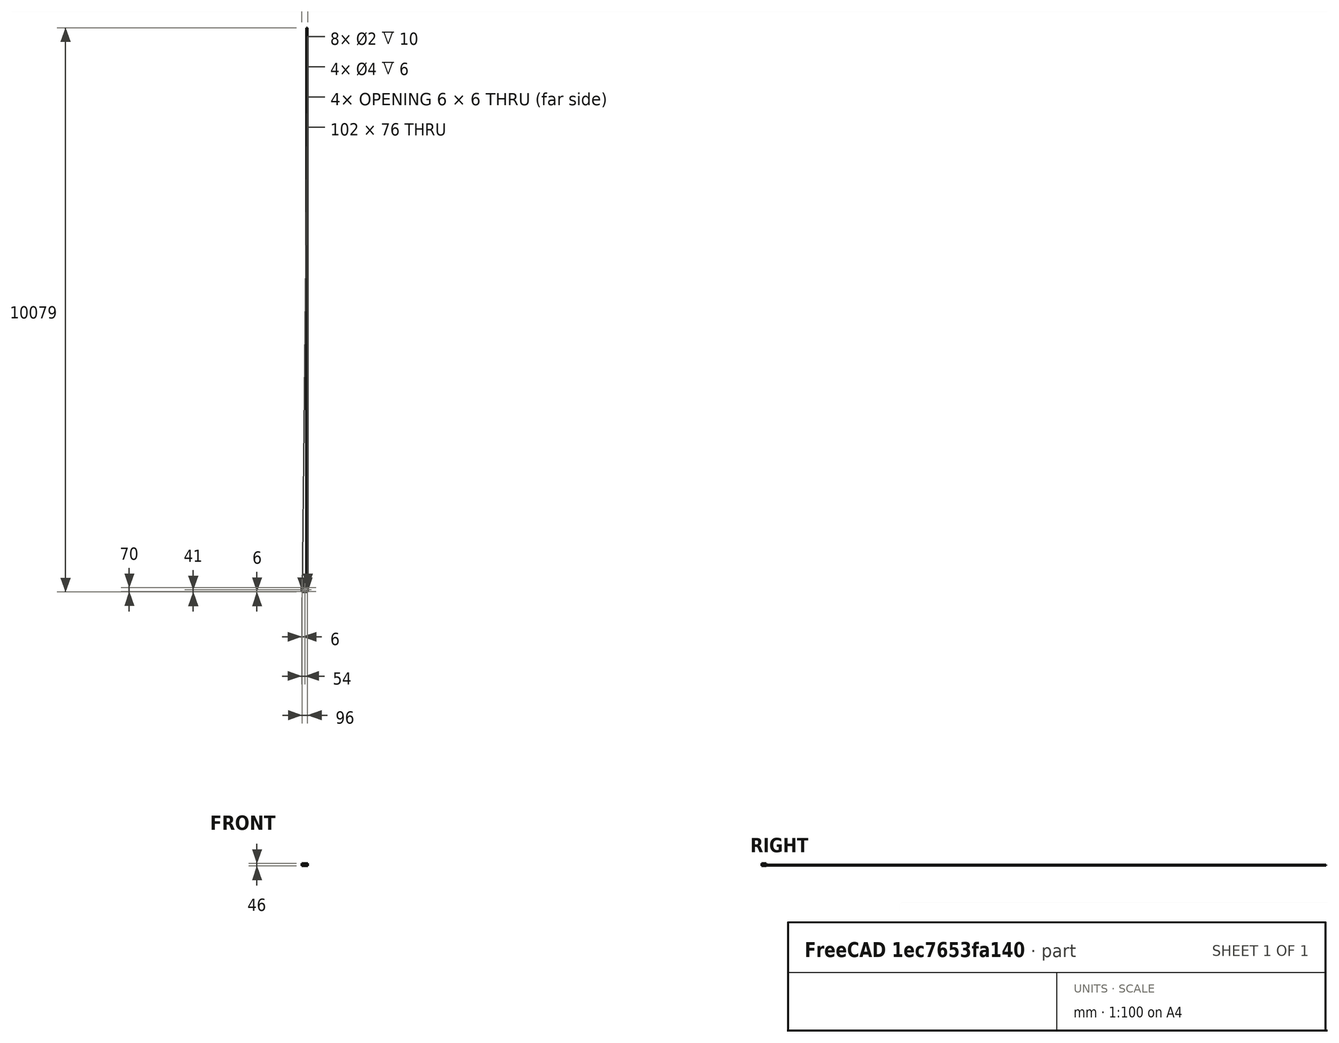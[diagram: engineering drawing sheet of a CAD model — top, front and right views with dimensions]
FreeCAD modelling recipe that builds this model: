
FCSTD DOCUMENT  (FreeCAD 0.16R6712 (Git))
Label: DMX_RGB_BOX
License: All rights reserved
LicenseURL: http://en.wikipedia.org/wiki/All_rights_reserved
objects: Part::Box×5, Part::Cut×5, Part::Cylinder×4, PartDesign::Chamfer×3, Part::Fillet×3, Sketcher::SketchObject×2, PartDesign::Pocket×2, PartDesign::Fillet×1, Part::MultiFuse×1, Mesh::Feature×1
note: 28 computed .brp shape members not serialized (recipe doc carries the construction recipe); baked Part::Feature solids carry a one-line shape summary decoded from their .brp

FEATURE [PartDesign::Chamfer] Chamfer  label="Deckel"
  Placement = pos=(0,82,46) rot=(1,0,0;3.14159rad)
  Size = 2
FEATURE [Part::Box] Box  label="Würfel"
  Height = 43
  Length = 108
  Width = 82
FEATURE [Part::Box] Box001  label="Würfel001"
  Height = 41
  Length = 102
  Placement = pos=(3,3,3) rot=(0,0,1;0rad)
  Width = 76
FEATURE [Part::Cut] Cut
  Base = -> Box
  Tool = -> Box001
FEATURE [PartDesign::Fillet] Fillet
  Placement = pos=(3,3,0) rot=(0,0,1;0rad)
  Radius = 3
FEATURE [Part::Box] Box003  label="Würfel003"
  Height = 35
  Length = 6
  Placement = pos=(3,73,0) rot=(0,0,1;0rad)
  Width = 6
FEATURE [Part::Box] Box004  label="Würfel004"
  Height = 35
  Length = 6
  Placement = pos=(99,3,0) rot=(0,0,1;0rad)
  Width = 6
FEATURE [Part::Box] Box005  label="Würfel005"
  Height = 35
  Length = 6
  Placement = pos=(99,73,0) rot=(0,0,1;0rad)
  Width = 6
FEATURE [Part::Fillet] Fillet001
  Base = -> Box003
  Edges = 1 edges r=3: [Edge5]
FEATURE [Part::Fillet] Fillet002
  Base = -> Box004
  Edges = 1 edges r=3: [Edge3]
FEATURE [Part::Fillet] Fillet003
  Base = -> Box005
  Edges = 1 edges r=3: [Edge1]
FEATURE [Part::Cylinder] Cylinder  label="Zylinder"
  Angle = 360
  Height = 10
  Placement = pos=(6,6,25) rot=(0,0,1;0rad)
  Radius = 1
FEATURE [Part::Cut] Cut001
  Base = -> Fillet
  Tool = -> Cylinder
FEATURE [Part::Cylinder] Cylinder001  label="Zylinder001"
  Angle = 360
  Height = 10
  Placement = pos=(6,76,25) rot=(0,0,1;0rad)
  Radius = 1
FEATURE [Part::Cut] Cut002
  Base = -> Fillet001
  Tool = -> Cylinder001
FEATURE [Part::Cylinder] Cylinder002  label="Zylinder002"
  Angle = 360
  Height = 10
  Placement = pos=(102,6,25) rot=(0,0,1;0rad)
  Radius = 1
FEATURE [Part::Cut] Cut003
  Base = -> Fillet002
  Tool = -> Cylinder002
FEATURE [Part::Cylinder] Cylinder003  label="Zylinder003"
  Angle = 360
  Height = 10
  Placement = pos=(102,76,25) rot=(0,0,1;0rad)
  Radius = 1
FEATURE [Part::Cut] Cut004
  Base = -> Fillet003
  Tool = -> Cylinder003
FEATURE [Part::MultiFuse] Fusion
  Shapes = -> [Cut,Cut001,Cut002,Cut003,Cut004]
FEATURE [Sketcher::SketchObject] Sketch
  Placement = pos=(0,0,3) rot=(0,0,1;0rad)
  Support = -> Fusion [Face17]
  sketch-geometry (8):
    g0: LineSegment [constr] StartX=11 StartY=71 StartZ=0 EndX=97 EndY=71 EndZ=0
    g1: LineSegment [constr] StartX=97 StartY=71 StartZ=0 EndX=97 EndY=11 EndZ=0
    g2: LineSegment [constr] StartX=97 StartY=11 StartZ=0 EndX=11 EndY=11 EndZ=0
    g3: LineSegment [constr] StartX=11 StartY=11 StartZ=0 EndX=11 EndY=71 EndZ=0
    g4: Circle CenterX=11 CenterY=71 CenterZ=0 NormalX=0 NormalY=0 NormalZ=1 Radius=1.75
    g5: Circle CenterX=11 CenterY=11 CenterZ=0 NormalX=0 NormalY=0 NormalZ=1 Radius=1.75
    g6: Circle CenterX=97 CenterY=71 CenterZ=0 NormalX=0 NormalY=0 NormalZ=1 Radius=1.75
    g7: Circle CenterX=97 CenterY=11 CenterZ=0 NormalX=0 NormalY=0 NormalZ=1 Radius=1.75
  constraints (20):
    c: Coincident(g0,g1)
    c: Coincident(g1,g2)
    c: Coincident(g2,g3)
    c: Coincident(g3,g0)
    c: Horizontal(g0)
    c: Horizontal(g2)
    c: Vertical(g1)
    c: Vertical(g3)
    c: DistanceX(g-1,g2) = 11
    c: DistanceY(g-1,g2) = 11
    c: DistanceX(g-1,g1) = 97
    c: DistanceY(g-1,g0) = 71
    c: Radius(g4) = 1.75
    c: Equal(g4,g5)
    c: Equal(g4,g6)
    c: Equal(g4,g7)
    c: Coincident(g4,g0)
    c: Coincident(g5,g2)
    c: Coincident(g6,g0)
    c: Coincident(g7,g1)
FEATURE [PartDesign::Pocket] Pocket
  Length = 5
  Sketch = -> Sketch
  Type = 1
FEATURE [PartDesign::Chamfer] Chamfer001
  Base = -> Pocket [Edge65]
  Size = 1
FEATURE [PartDesign::Chamfer] Chamfer002
  Base = -> Chamfer001 [Edge49,Edge50,Edge51]
  Size = 1
FEATURE [Sketcher::SketchObject] Sketch001
  Placement = pos=(0,79,0) rot=(1,0,0;1.5708rad)
  Support = -> Chamfer002 [Face12]
  sketch-geometry (1):
    g0: Circle CenterX=90 CenterY=15 CenterZ=0 NormalX=0 NormalY=0 NormalZ=1 Radius=7.5
  constraints (3):
    c: Radius(g0) = 7.5
    c: DistanceY(g-1,g0) = 15
    c: DistanceX(g-1,g0) = 90
FEATURE [PartDesign::Pocket] Pocket001
  Length = 5
  Sketch = -> Sketch001
  Type = 1
FEATURE [Mesh::Feature] Mesh  label="Pocket001 (Meshed)"
